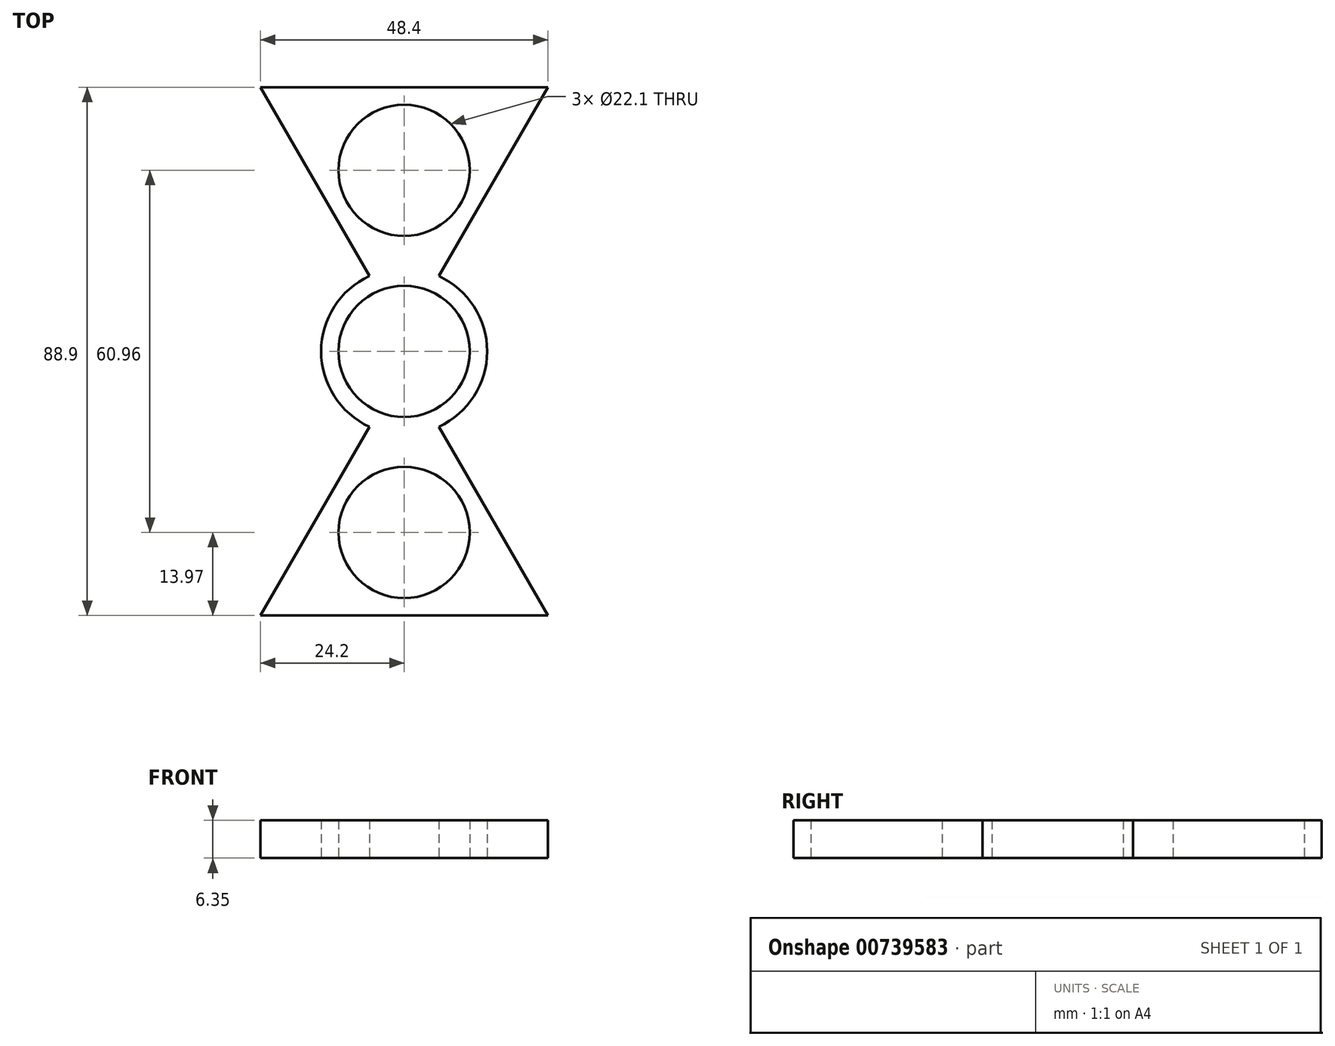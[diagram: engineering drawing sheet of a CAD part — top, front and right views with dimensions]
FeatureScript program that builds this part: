
annotation { "Feature Type Name" : "Feature", "Feature Type Description" : "" }
export const myFeature = defineFeature(function(context is Context, id is Id, definition is map)
    precondition{}
    {
        {
            var Q0;
            Q0=qCreatedBy(makeId("Top.planeOp"),FACE);
            var sketch = newSketch(context, id + "F0", { "sketchPlane" : qUnion([Q0])});
            skCircle(sketch, "E0", {"center": v(0, 0) * mm, "radius": 13.97 * mm});
            skCircle(sketch, "E1", {"center": v(0, 0) * mm, "radius": 11.05 * mm});
            skLineSegment(sketch, "E2", {"start": v(0, 0) * mm, "end": v(0, 30.48) * mm});
            skCircle(sketch, "E3", {"center": v(0, 30.48) * mm, "radius": 11.05 * mm});
            skCircle(sketch, "E4", {"center": v(0, 30.48) * mm, "radius": 13.97 * mm});
            skLineSegment(sketch, "E5", {"start": v(0, 0) * mm, "end": v(0, -30.48) * mm});
            skCircle(sketch, "E6", {"center": v(0, -30.48) * mm, "radius": 13.97 * mm});
            skCircle(sketch, "E7", {"center": v(0, -30.48) * mm, "radius": 11.05 * mm});
            skCircle(sketch, "E8.cCircle", {"center": v(0, -30.48) * mm, "radius": 13.97 * mm, "construction": true});
            skLineSegment(sketch, "E8.0", {"start": v(24.2, -44.45) * mm, "end": v(-24.2, -44.45) * mm});
            skLineSegment(sketch, "E8.1", {"start": v(-24.2, -44.45) * mm, "end": v(-5.86, -12.68) * mm});
            skLineSegment(sketch, "E8.2", {"start": v(5.86, -12.68) * mm, "end": v(24.2, -44.45) * mm});
            skPoint(sketch, "E8.0.midPoint", {"position": v(0, -44.45) * mm});
            skLineSegment(sketch, "E9.0", {"start": v(-24.2, 44.45) * mm, "end": v(24.2, 44.45) * mm});
            skLineSegment(sketch, "E9.1", {"start": v(24.2, 44.45) * mm, "end": v(5.86, 12.68) * mm});
            skPoint(sketch, "E9.0.midPoint", {"position": v(0, 44.45) * mm});
            skLineSegment(sketch, "E10.trimOffspring", {"start": v(-5.86, 12.68) * mm, "end": v(-24.2, 44.45) * mm});
            skPoint(sketch, "E11.orphan", {"position": v(0, -2.54) * mm});
            skSolve(sketch);
        }
        {
            var Q0;
            Q0 = qSketchRegion(id + "F0", true);
            extrude(context, id + "F1", {"entities" : qUnion([Q0]), "depth" : 6.35 * mm, "offsetDistance" : 25.4 * mm});
        }
    });
